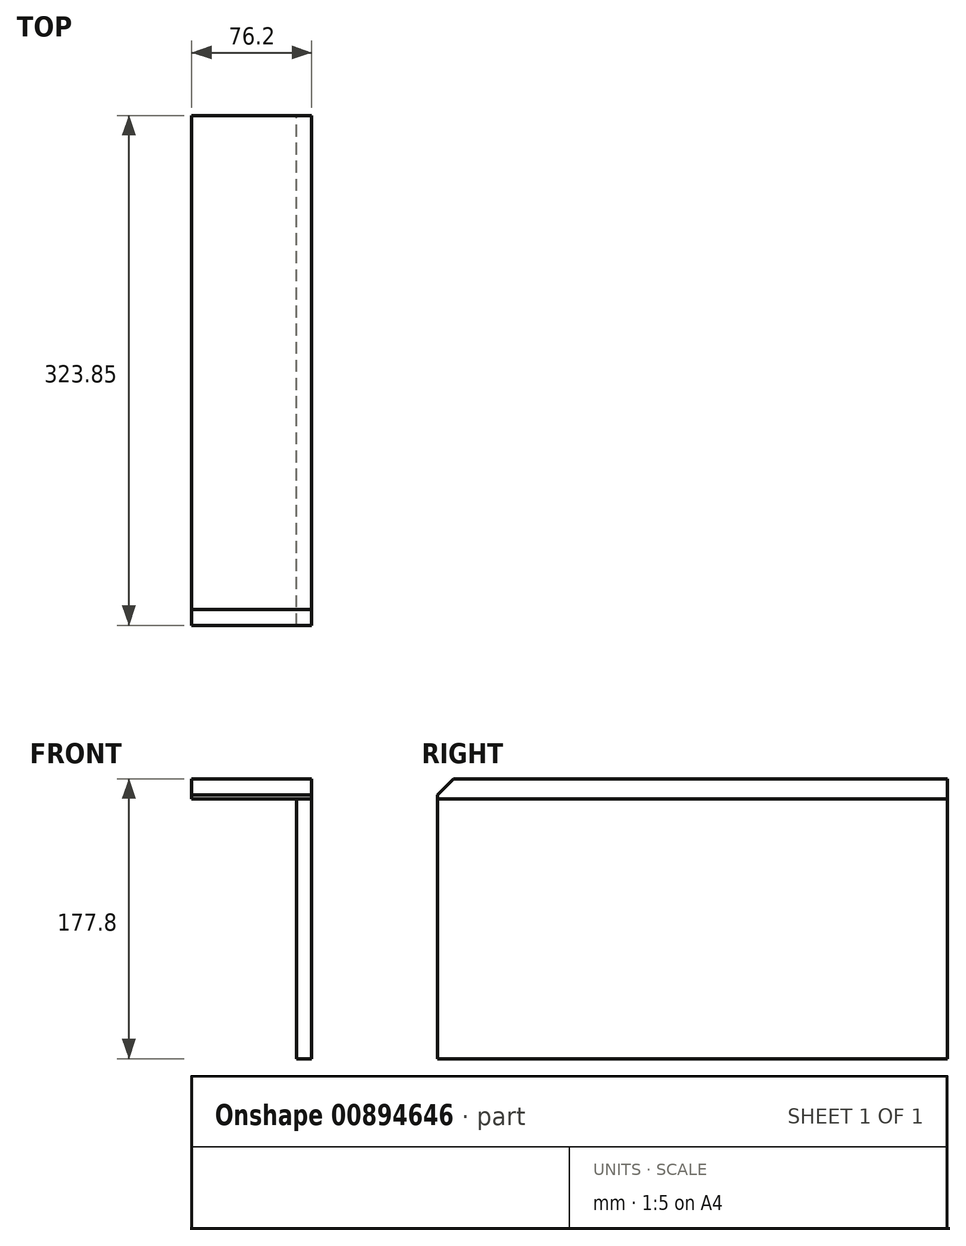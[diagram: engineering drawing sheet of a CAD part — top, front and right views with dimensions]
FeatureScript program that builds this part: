
annotation { "Feature Type Name" : "Feature", "Feature Type Description" : "" }
export const myFeature = defineFeature(function(context is Context, id is Id, definition is map)
    precondition{}
    {
        {
            var Q0;
            Q0=qCreatedBy(makeId("Front.planeOp"),FACE);
            var sketch = newSketch(context, id + "F0", { "sketchPlane" : qUnion([Q0])});
            skLineSegment(sketch, "E0", {"start": v(-9.53, 0) * mm, "end": v(0, 0) * mm});
            skLineSegment(sketch, "E1", {"start": v(0, 0) * mm, "end": v(0, 177.8) * mm});
            skLineSegment(sketch, "E2", {"start": v(0, 177.8) * mm, "end": v(-76.2, 177.8) * mm});
            skLineSegment(sketch, "E3", {"start": v(-76.2, 177.8) * mm, "end": v(-76.2, 165.1) * mm});
            skLineSegment(sketch, "E4", {"start": v(-76.2, 165.1) * mm, "end": v(-9.53, 165.1) * mm});
            skLineSegment(sketch, "E5", {"start": v(-9.53, 165.1) * mm, "end": v(-9.53, 0) * mm});
            skLineSegment(sketch, "E6", {"start": v(-9.53, 165.1) * mm, "end": v(0, 165.1) * mm});
            skSolve(sketch);
        }
        {
            var Q0;
            Q0=makeQuery(id+"F0.imprint","IMPRINT",FACE,{"disambiguationData":[TD([[makeQuery(id+"F0.imprint","IMPRINT",EDGE,{"derivedFrom":sQuery(id+"F0.wireOp",EDGE,"E0")}),1.0]])]});
            extrude(context, id + "F1", {"entities" : qUnion([Q0]), "depth" : 323.85 * mm, "offsetDistance" : 25.4 * mm});
        }
        {
            var Q0;
            {var subQ0=sQuery(id+"F0.wireOp",EDGE,"E2");Q0=makeQuery(id+"F0.imprint","IMPRINT",FACE,{"disambiguationData":[TD([[makeQuery(id+"F0.imprint","IMPRINT",EDGE,{"derivedFrom":subQ0}),1.0]])]});}
            var Q1;
            Q1=makeQuery(id+"F1.opExtrude","CAP_FACE",FACE,{"disambiguationData":[OSD([sQuery(id+"F0.wireOp",EDGE,"E0"),sQuery(id+"F0.wireOp",EDGE,"E1"),sQuery(id+"F0.wireOp",EDGE,"E5"),sQuery(id+"F0.wireOp",EDGE,"E6")])],"isStart":false});
            extrude(context, id + "F2", {"entities" : qUnion([Q0]), "endBound" : BoundingType.UP_TO_SURFACE, "depth" : 25.4 * mm, "endBoundEntityFace" : qUnion([Q1]), "offsetDistance" : 25.4 * mm});
        }
        {
            var Q0;
            Q0=makeQuery(id+"F2.opExtrude","CAP_EDGE",EDGE,{"disambiguationData":[OSD([sQuery(id+"F0.wireOp",EDGE,"E2")])],"isStart":false});
            chamfer(context, id + "F3", {"entities" : qUnion([Q0]), "width" : 10.16 * mm, "tangentPropagation" : true});
        }
    });
